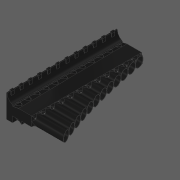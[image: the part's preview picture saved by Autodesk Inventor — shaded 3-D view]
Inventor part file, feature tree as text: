
AUTODESK INVENTOR PART (.ipt)
format: ipt  version: 2020 (Build 240168000, 168)  size: 2,600,448 bytes
history: native  units: in
note: dims shown in document units (in); Inventor stores cm internally (conversion verified against a paired STEP export)
features: other x16, extrude x8, fillet x2, pattern_linear x1, loft x1
ambient origin geometry x8: Origin, YZ Plane, XZ Plane, XY Plane, X Axis, Y Axis, Z Axis, Center Point
bodies: Solid1 (feature_tree)
feature tree (28):
  other  "Midplane"
  extrude  "Block"  TaperAngle=0.0deg  [1 undecoded]
  extrude  "Hinge Protrusion"  Depth=4.7244in
  other  "Resonator Profile"
  extrude  "Resonator"  Depth=0.3153in TaperAngle=0.0deg
  extrude  "Resonator Cut"  Depth=0.4921in
  extrude  "Duct Cavity"  TaperAngle=0.0deg  [1 undecoded]
  extrude  "Duct Entrance"  Depth=0.4921in
  other  "Fitting"
  extrude  "Slit"  Depth=2.3498in TaperAngle=0.0deg
  fillet  "Fillet2"  Radius=0.3056in
  pattern_linear  "Repeat Keys"  Spacing1=0.1969in  [1 undecoded]
  other  "Edge Loft From"
  other  "Edge Loft To"
  loft  "Edge Cut Loft"
  extrude  "Tube Length Cut"  Depth=0.9843in
  fillet  "Edge Fillet"  Radius=0.0315in
  other  "Tube Length Curve"
  other  "Block Profile"
  other  "Fitting Sketch"
  other  "Duct Cavity Profile"
  other  "Duct Entrance Sketch"
  other  "Edge Cut Loft From"
  other  "Edge Cut Loft To"
  other  "2D Equation Curve5"
  other  "2D Equation Curve7"
  other  "Slit Sketch"
  other  "Hinge Protrusion Sketch"
note: 3 required parameter values undecoded (feature->parameter linkage not recoverable at this tier; creation-order binding heuristic only, values carry confidence <= 0.55)
